# Revit family: Ecoline Wall Mount Grab Bar  family
name_source: partatom
category: Furniture
revit_build: Autodesk Revit 2018 (Build: 20170223_1515(x64)
units: mm (PartAtom-declared; Revit-internal decimal feet)

## family parameters
Always vertical = Yes
Cut with Voids When Loaded = No
OmniClass Number = 23.40.20.00
OmniClass Title = General Furniture and Specialties
Room Calculation Point = No
Shared = No
Work Plane-Based = No

## types (6) — shared parameters
Model = C8871-C8876 Stainless Steel
URL = http://www.kromedispense.com

## type names (no varying parameters)
- C8873-12"-Economy Wall Mount Grab Bar, Stainless Steel
- C8871-18"-Economy Wall Mount Grab Bar, Stainless Steel
- C8872-9"-Economy Wall Mount Grab Bar, Stainless Steel
- C8874-24"-Economy Wall Mount Grab Bar, Stainless Steel
- C8875-36"-Economy Wall Mount Grab Bar, Stainless Steel
- C8876-48"-Economy Wall Mount Grab Bar, Stainless Steel

## geometry (parser evidence)
native form markers: Sweep x2
no freeform markers — native parametric forms only
